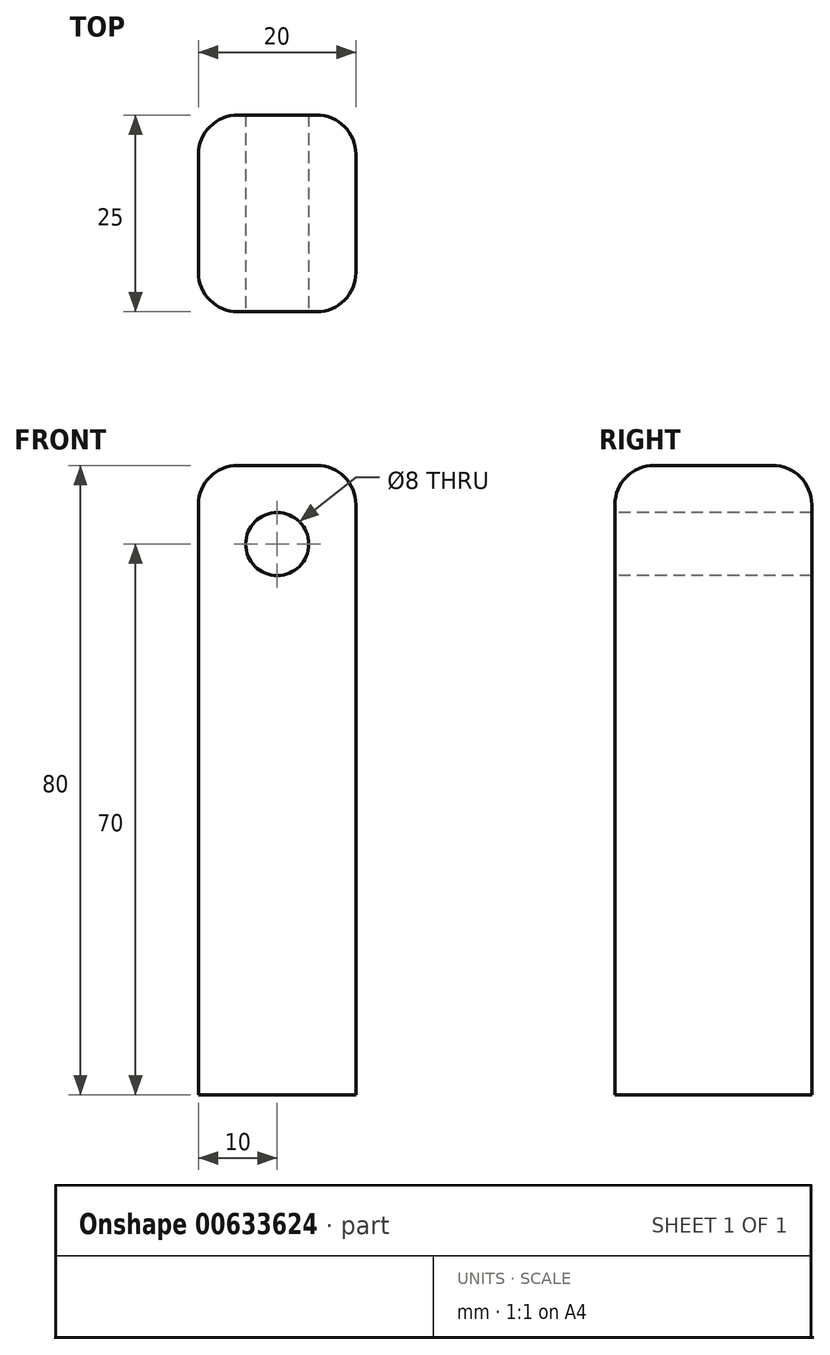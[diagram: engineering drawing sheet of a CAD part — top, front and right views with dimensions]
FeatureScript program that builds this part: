
annotation { "Feature Type Name" : "Feature", "Feature Type Description" : "" }
export const myFeature = defineFeature(function(context is Context, id is Id, definition is map)
    precondition{}
    {
        {
            var Q0;
            Q0=qCreatedBy(makeId("Front.planeOp"),FACE);
            var sketch = newSketch(context, id + "F0", { "sketchPlane" : qUnion([Q0])});
            skLineSegment(sketch, "E0", {"start": v(-10, 40) * mm, "end": v(10, 40) * mm});
            skLineSegment(sketch, "E1", {"start": v(10, 40) * mm, "end": v(10, -40) * mm});
            skLineSegment(sketch, "E2", {"start": v(10, -40) * mm, "end": v(-10, -40) * mm});
            skLineSegment(sketch, "E3", {"start": v(-10, -40) * mm, "end": v(-10, 40) * mm});
            skSolve(sketch);
        }
        {
            var Q0;
            Q0=qSketchRegion(id+"F0",true);
            extrude(context, id + "F1", {"entities" : qUnion([Q0]), "depth" : 25 * mm, "offsetDistance" : 25 * mm});
        }
        {
            var Q0;
            Q0=makeQuery(id+"F1.opExtrude","CAP_FACE",FACE,{"disambiguationData":[OSD([sQuery(id+"F0.wireOp",EDGE,"E0"),sQuery(id+"F0.wireOp",EDGE,"E1"),sQuery(id+"F0.wireOp",EDGE,"E2"),sQuery(id+"F0.wireOp",EDGE,"E3")])],"isStart":false});
            var sketch = newSketch(context, id + "F2", { "sketchPlane" : qUnion([Q0])});
            skCircle(sketch, "E4", {"center": v(0, 30) * mm, "radius": 4 * mm});
            skSolve(sketch);
        }
        {
            var Q0;
            Q0=qSketchRegion(id+"F2",true);
            extrude(context, id + "F3", {"entities" : qUnion([Q0]), "operationType" : NewBodyOperationType.REMOVE, "oppositeDirection" : true, "depth" : 25 * mm, "offsetDistance" : 25 * mm});
        }
        {
            var Q0;
            Q0=makeQuery(id+"F1.opExtrude","CAP_EDGE",EDGE,{"disambiguationData":[OSD([sQuery(id+"F0.wireOp",EDGE,"E0")])],"isStart":false});
            var Q1;
            Q1=makeQuery(id+"F1.opExtrude","SWEPT_EDGE",EDGE,{"disambiguationData":[OSD([sQuery(id+"F0.wireOp",EDGE,"E0"),sQuery(id+"F0.wireOp",EDGE,"E1")])]});
            var Q2;
            Q2=makeQuery(id+"F1.opExtrude","CAP_EDGE",EDGE,{"disambiguationData":[OSD([sQuery(id+"F0.wireOp",EDGE,"E0")])],"isStart":true});
            var Q3;
            Q3=makeQuery(id+"F1.opExtrude","SWEPT_EDGE",EDGE,{"disambiguationData":[OSD([sQuery(id+"F0.wireOp",EDGE,"E0"),sQuery(id+"F0.wireOp",EDGE,"E3")])]});
            var Q4;
            Q4=makeQuery(id+"F1.opExtrude","CAP_EDGE",EDGE,{"disambiguationData":[OSD([sQuery(id+"F0.wireOp",EDGE,"E1")])],"isStart":false});
            var Q5;
            Q5=makeQuery(id+"F1.opExtrude","CAP_EDGE",EDGE,{"disambiguationData":[OSD([sQuery(id+"F0.wireOp",EDGE,"E3")])],"isStart":true});
            var Q6;
            Q6=makeQuery(id+"F1.opExtrude","CAP_EDGE",EDGE,{"disambiguationData":[OSD([sQuery(id+"F0.wireOp",EDGE,"E1")])],"isStart":true});
            var Q7;
            Q7=makeQuery(id+"F1.opExtrude","CAP_EDGE",EDGE,{"disambiguationData":[OSD([sQuery(id+"F0.wireOp",EDGE,"E3")])],"isStart":false});
            fillet(context, id + "F4", {"entities" : qUnion([Q0, Q1, Q2, Q3, Q4, Q5, Q6, Q7]), "radius" : 5 * mm, "tangentPropagation" : true, "allowEdgeOverflow" : false});
        }
    });
